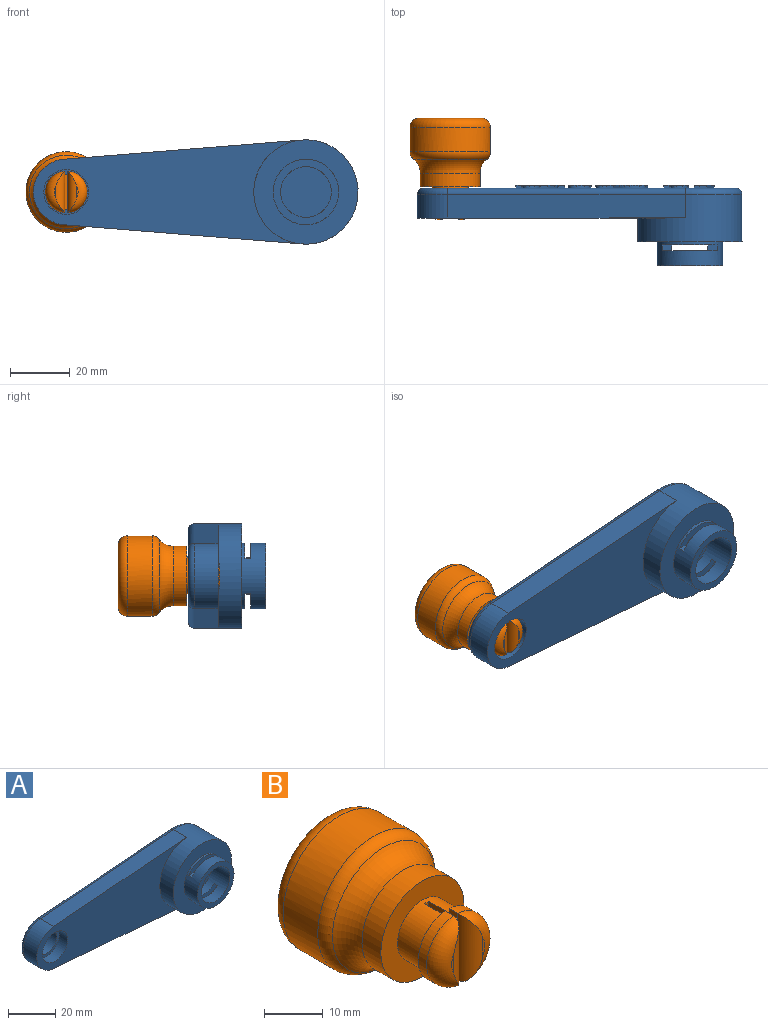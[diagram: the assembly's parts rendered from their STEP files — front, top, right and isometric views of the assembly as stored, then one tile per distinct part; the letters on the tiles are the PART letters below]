
ASSEMBLY  parts=2 mates=1
PART A: 165 faces, bbox 111.3x27x37.9 mm
  f0: plane 104.91x31mm, normal (0,1,0), area 2040.8mm2, adj f22,f23,f24,f25,f27,f28,f29,f30
  f1: cylinder r=7.5mm len=15mm, axis (0,1,0), area 235.6mm2, adj f8,f26
  f2: cylinder r=11mm len=22mm, axis (0,1,0), area 466.1mm2, adj f9,f10,f12,f13,f14,f16,f17,f18
  f3: cylinder r=8.5mm len=17mm, axis (0,1,0), area 534mm2, adj f10,f11,f13,f14,f15,f16,f18,f19
  f4: cylinder r=17.5mm len=35mm, axis (0,1,0), area 1344.7mm2, adj f5,f7,f8,f9,f22
  f5: plane 79.73x8mm, normal (-0.08,0,1), area 639.9mm2, adj f4,f6,f8,f23
  f6: cylinder r=11mm len=21.93mm, axis (0,1,0), area 262.2mm2, adj f5,f7,f8,f25
  f7: plane 79.73x8mm, normal (-0.08,0,-1), area 639.9mm2, adj f4,f6,f8,f24
  f8: plane 89.84x34.86mm, normal (0,-1,0), area 1831.5mm2, adj f1,f4,f5,f6,f7
  f9: plane 35x35mm, normal (0,-1,0), area 582mm2, adj f2,f4
  f10: plane 22x22mm, normal (0,-1,0), area 153.2mm2, adj f2,f3
  f11: plane 17x17mm, normal (0,-1,0), area 227mm2, adj f3
  f12: plane 2x0.14mm, normal (-1,0,0), area 0.3mm2, adj f2,f13,f14,f15
  f13: plane 18.35x5mm, normal (0,-1,0), area 44.2mm2, adj f2,f3,f12,f15,f16
  f14: plane 18.35x5mm, normal (0,1,0), area 44.2mm2, adj f2,f3,f12,f15,f16
  f15: plane 3.11x2mm, normal (0,0,-1), area 6.2mm2, adj f3,f12,f13,f14
  f16: plane 3.2x2mm, normal (0,0,-1), area 6.4mm2, adj f2,f3,f13,f14
  f17: plane 2x0.14mm, normal (-1,0,0), area 0.3mm2, adj f2,f18,f19,f21
  f18: plane 18.35x5mm, normal (0,-1,0), area 44.2mm2, adj f2,f3,f17,f20,f21
  f19: plane 18.35x5mm, normal (0,1,0), area 44.2mm2, adj f2,f3,f17,f20,f21
  f20: plane 3.2x2mm, normal (0,0,1), area 6.4mm2, adj f2,f3,f18,f19
  f21: plane 3.11x2mm, normal (0,0,1), area 6.2mm2, adj f3,f17,f18,f19
  f22: torus R=15.5mm, axis (0,-1,0), area 175.1mm2, adj f0,f4,f23,f24
  f23: cylinder r=2mm len=79.9mm, axis (-1,0,-0.08), area 251.3mm2, adj f0,f5,f22,f25
  f24: cylinder r=2mm len=79.9mm, axis (1,0,-0.08), area 251.3mm2, adj f0,f7,f22,f25
  f25: torus R=9mm, axis (0,-1,0), area 96.2mm2, adj f0,f6,f23,f24
  f26: plane 15x15mm, normal (0,-1,0), area 63.6mm2, adj f1,f27
  f27: cylinder r=6mm len=12mm, axis (0,-1,0), area 188.5mm2, adj f0,f26
  f28: plane 11.28x2.38mm, normal (0.98,0,0.21), area 11.5mm2, adj f0,f29,f33,f34
  f29: plane 6.3x1mm, normal (0,0,-1), area 6.3mm2, adj f0,f28,f30,f34
  f30: plane 1.97x1mm, normal (-0.98,0,-0.21), area 2mm2, adj f0,f29,f31,f34
  f31: plane 3.95x1mm, normal (0,0,1), area 3.9mm2, adj f0,f30,f32,f34
  f32: plane 9.3x1.97mm, normal (-0.98,0,-0.21), area 9.5mm2, adj f0,f31,f33,f34
  f33: plane 2.36x1mm, normal (0,0,1), area 2.4mm2, adj f0,f28,f32,f34
  f34: plane 11.28x6.72mm, normal (0,1,0), area 34.4mm2, adj f28,f29,f30,f31,f32,f33
  f35: extruded ~1.02x1mm, area 1.2mm2, adj f36,f59,f60,f61
  f36: extruded ~1x0.74mm, area 0.8mm2, adj f35,f37,f60,f61
  f37: extruded ~1.02x1mm, area 1.1mm2, adj f36,f38,f60,f61
  f38: extruded ~1.8x1mm, area 1.8mm2, adj f37,f39,f60,f61
  f39: extruded ~1.47x1mm, area 1.7mm2, adj f38,f40,f60,f61
  f40: extruded ~1x1mm, area 1.2mm2, adj f39,f41,f60,f61
  f41: extruded ~1x0.78mm, area 0.9mm2, adj f40,f42,f60,f61
  f42: extruded ~1x0.91mm, area 1mm2, adj f41,f43,f60,f61
  f43: extruded ~2x1mm, area 2mm2, adj f42,f59,f60,f61
  f44: extruded ~1.79x1mm, area 2mm2, adj f0,f45,f58,f60
  f45: extruded ~2.46x1.27mm, area 2.9mm2, adj f0,f44,f46,f60
  f46: plane 1x0.03mm, normal (0,0,-1), area 0mm2, adj f0,f45,f47,f60
  f47: plane 1.12x1mm, normal (1,0,0.1), area 1.1mm2, adj f0,f46,f48,f60
  f48: plane 1.77x1mm, normal (0,0,-1), area 1.8mm2, adj f0,f47,f49,f60
  f49: plane 8.62x1.84mm, normal (-0.98,0,-0.21), area 8.8mm2, adj f0,f48,f50,f60
  f50: plane 1.79x1mm, normal (0,0,1), area 1.8mm2, adj f0,f49,f51,f60
  f51: plane 1.1x1mm, normal (0.93,0,0.37), area 1.2mm2, adj f0,f50,f52,f60
  f52: plane 1x0.06mm, normal (0,0,1), area 0.1mm2, adj f0,f51,f53,f60
  f53: extruded ~1x0.94mm, area 1.3mm2, adj f0,f52,f54,f60
  f54: extruded ~1.29x1mm, area 1.3mm2, adj f0,f53,f55,f60
  f55: extruded ~1.98x1mm, area 2.2mm2, adj f0,f54,f56,f60
  f56: extruded ~2.14x1.46mm, area 2.6mm2, adj f0,f55,f57,f60
  f57: extruded ~2.91x1mm, area 3mm2, adj f0,f56,f58,f60
  f58: extruded ~2.3x1mm, area 2.4mm2, adj f0,f44,f57,f60
  f59: extruded ~1.4x1mm, area 1.6mm2, adj f35,f43,f60,f61
  f60: plane 8.94x8.42mm, normal (0,1,0), area 46.1mm2, adj f35,f36,f37,f38,f39,f40,f41,f42
  f61: plane 5.18x3.12mm, normal (0,1,0), area 12mm2, adj f35,f36,f37,f38,f39,f40,f41,f42
  f62: extruded ~1.83x1mm, area 2mm2, adj f0,f63,f79,f80
  f63: extruded ~1.06x1mm, area 1.1mm2, adj f0,f62,f64,f80
  f64: extruded ~1.35x1mm, area 1.5mm2, adj f0,f63,f65,f80
  f65: plane 1.93x1mm, normal (-0.9,0,-0.43), area 2.1mm2, adj f0,f64,f66,f80
  f66: extruded ~1.6x1mm, area 1.7mm2, adj f0,f65,f67,f80
  f67: extruded ~1.71x1mm, area 1.7mm2, adj f0,f66,f68,f80
  f68: extruded ~3.09x1mm, area 3.3mm2, adj f0,f67,f69,f80
  f69: extruded ~2.58x2.14mm, area 3.4mm2, adj f0,f68,f70,f80
  f70: extruded ~3.72x1mm, area 3.8mm2, adj f0,f69,f71,f80
  f71: extruded ~3.27x1.09mm, area 3.5mm2, adj f0,f70,f72,f80
  f72: extruded ~3.05x1.15mm, area 3.4mm2, adj f0,f71,f73,f80
  f73: extruded ~3.09x1mm, area 3.2mm2, adj f0,f72,f74,f80
  f74: plane 2.01x1mm, normal (-1,0,0), area 2mm2, adj f0,f73,f75,f80
  f75: extruded ~2.61x1mm, area 2.7mm2, adj f0,f74,f76,f80
  f76: extruded ~1.69x1mm, area 1.9mm2, adj f0,f75,f77,f80
  f77: extruded ~1.91x1mm, area 2mm2, adj f0,f76,f78,f80
  f78: extruded ~2.61x1mm, area 2.7mm2, adj f0,f77,f79,f80
  f79: extruded ~1.84x1.31mm, area 2.3mm2, adj f0,f62,f78,f80
  f80: plane 11.61x9.35mm, normal (0,1,0), area 43.6mm2, adj f62,f63,f64,f65,f66,f67,f68,f69
  f81: plane 2.32x1mm, normal (0,0,-1), area 2.3mm2, adj f0,f82,f99,f100
  f82: plane 4.91x1.03mm, normal (-0.98,0,-0.2), area 5mm2, adj f0,f81,f83,f100
  f83: extruded ~1.39x1mm, area 1.4mm2, adj f0,f82,f84,f100
  f84: extruded ~1.84x1mm, area 2mm2, adj f0,f83,f85,f100
  f85: extruded ~1.65x1mm, area 1.8mm2, adj f0,f84,f86,f100
  f86: extruded ~1.36x1mm, area 1.4mm2, adj f0,f85,f87,f100
  f87: extruded ~1.07x1mm, area 1.4mm2, adj f0,f86,f88,f100
  f88: plane 1x0.06mm, normal (0,0,1), area 0.1mm2, adj f0,f87,f89,f100
  f89: extruded ~2.38x1mm, area 2.5mm2, adj f0,f88,f90,f100
  f90: extruded ~2.14x1mm, area 2.2mm2, adj f0,f89,f91,f100
  f91: plane 2.32x1mm, normal (0,0,1), area 2.3mm2, adj f0,f90,f92,f100
  f92: plane 12x2.54mm, normal (0.98,0,0.21), area 12.3mm2, adj f0,f91,f93,f100
  f93: plane 2.32x1mm, normal (0,0,-1), area 2.3mm2, adj f0,f92,f94,f100
  f94: plane 3.57x1mm, normal (-0.98,0,-0.21), area 3.7mm2, adj f0,f93,f95,f100
  f95: extruded ~2.45x1mm, area 2.6mm2, adj f0,f94,f96,f100
  f96: extruded ~1.29x1mm, area 1.6mm2, adj f0,f95,f97,f100
  f97: extruded ~1x0.95mm, area 1.4mm2, adj f0,f96,f98,f100
  f98: extruded ~1x0.92mm, area 0.9mm2, adj f0,f97,f99,f100
  f99: plane 5.04x1.06mm, normal (0.98,0,0.21), area 5.1mm2, adj f0,f81,f98,f100
  f100: plane 12x8.45mm, normal (0,1,0), area 51.5mm2, adj f81,f82,f83,f84,f85,f86,f87,f88
  f101: extruded ~2.52x1mm, area 2.7mm2, adj f0,f102,f124,f125
  f102: extruded ~3.01x1mm, area 3.1mm2, adj f0,f101,f103,f125
  f103: plane 1.75x1mm, normal (-1,0,0), area 1.8mm2, adj f0,f102,f104,f125
  f104: extruded ~1.33x1mm, area 1.4mm2, adj f0,f103,f105,f125
  f105: extruded ~1.22x1mm, area 1.2mm2, adj f0,f104,f106,f125
  f106: extruded ~1.14x1mm, area 1.2mm2, adj f0,f105,f107,f125
  f107: extruded ~1.11x1mm, area 1.2mm2, adj f0,f106,f108,f125
  f108: plane 1x0.16mm, normal (-1,0,0), area 0.2mm2, adj f0,f107,f109,f125
  f109: plane 1x0.16mm, normal (-1,0,-0.09), area 0.2mm2, adj f0,f108,f110,f125
  f110: plane 1x0.4mm, normal (0,0,-1), area 0.4mm2, adj f0,f109,f111,f125
  f111: extruded ~3.68x1mm, area 3.8mm2, adj f0,f110,f112,f125
  f112: extruded ~2.22x1.29mm, area 2.7mm2, adj f0,f111,f113,f125
  f113: extruded ~1.72x1mm, area 2mm2, adj f0,f112,f114,f125
  f114: extruded ~2.13x1mm, area 2.3mm2, adj f0,f113,f115,f125
  f115: extruded ~2.46x1mm, area 2.6mm2, adj f0,f114,f116,f125
  f116: extruded ~2.01x1.72mm, area 2.7mm2, adj f0,f115,f117,f125
  f117: extruded ~2.91x1mm, area 3mm2, adj f0,f116,f124,f125
  f118: extruded ~1.28x1mm, area 1.5mm2, adj f119,f123,f125,f126
  f119: extruded ~1x0.81mm, area 1.3mm2, adj f118,f120,f125,f126
  f120: extruded ~1.01x1mm, area 1.3mm2, adj f119,f121,f125,f126
  f121: extruded ~1.86x1mm, area 1.9mm2, adj f120,f122,f125,f126
  f122: plane 1x0.35mm, normal (0,0,1), area 0.3mm2, adj f121,f123,f125,f126
  f123: extruded ~1.5x1mm, area 1.7mm2, adj f118,f122,f125,f126
  f124: extruded ~2.46x1mm, area 2.7mm2, adj f0,f101,f117,f125
  f125: plane 8.94x7.71mm, normal (0,1,0), area 41.7mm2, adj f101,f102,f103,f104,f105,f106,f107,f108
  f126: plane 2.88x2.12mm, normal (0,1,0), area 4.2mm2, adj f118,f119,f120,f121,f122,f123
  f127: extruded ~1.72x1mm, area 1.9mm2, adj f0,f128,f136,f137
  f128: plane 1x0.05mm, normal (0,0,1), area 0mm2, adj f0,f127,f129,f137
  f129: extruded ~1.78x1mm, area 1.8mm2, adj f0,f128,f130,f137
  f130: plane 4.52x1mm, normal (-1,0,0.08), area 4.5mm2, adj f0,f129,f131,f137
  f131: plane 2.28x1mm, normal (0,0,1), area 2.3mm2, adj f0,f130,f132,f137
  f132: plane 8.62x1.06mm, normal (0.99,0,-0.12), area 8.7mm2, adj f0,f131,f133,f137
  f133: plane 2.49x1mm, normal (0,0,-1), area 2.5mm2, adj f0,f132,f134,f137
  f134: plane 8.62x4.66mm, normal (-0.88,0,-0.48), area 9.8mm2, adj f0,f133,f135,f137
  f135: plane 2.49x1mm, normal (0,0,1), area 2.5mm2, adj f0,f134,f136,f137
  f136: plane 4.58x2.29mm, normal (0.89,0,0.45), area 5.1mm2, adj f0,f127,f135,f137
  f137: plane 8.62x8.21mm, normal (0,1,0), area 35.7mm2, adj f127,f128,f129,f130,f131,f132,f133,f134
  f138: extruded ~1.02x1mm, area 1.2mm2, adj f139,f162,f163,f164
  f139: extruded ~1x0.74mm, area 0.8mm2, adj f138,f140,f163,f164
  f140: extruded ~1.02x1mm, area 1.1mm2, adj f139,f141,f163,f164
  f141: extruded ~1.8x1mm, area 1.8mm2, adj f140,f142,f163,f164
  f142: extruded ~1.47x1mm, area 1.7mm2, adj f141,f143,f163,f164
  f143: extruded ~1x1mm, area 1.2mm2, adj f142,f144,f163,f164
  f144: extruded ~1x0.78mm, area 0.9mm2, adj f143,f145,f163,f164
  f145: extruded ~1x0.91mm, area 1mm2, adj f144,f146,f163,f164
  f146: extruded ~2x1mm, area 2mm2, adj f145,f162,f163,f164
  f147: extruded ~1.79x1mm, area 2mm2, adj f0,f148,f161,f163
  f148: extruded ~2.46x1.27mm, area 2.9mm2, adj f0,f147,f149,f163
  f149: plane 1x0.03mm, normal (0,0,-1), area 0mm2, adj f0,f148,f150,f163
  f150: plane 1.12x1mm, normal (1,0,0.1), area 1.1mm2, adj f0,f149,f151,f163
  f151: plane 1.77x1mm, normal (0,0,-1), area 1.8mm2, adj f0,f150,f152,f163
  f152: plane 8.62x1.84mm, normal (-0.98,0,-0.21), area 8.8mm2, adj f0,f151,f153,f163
  f153: plane 1.79x1mm, normal (0,0,1), area 1.8mm2, adj f0,f152,f154,f163
  f154: plane 1.1x1mm, normal (0.93,0,0.37), area 1.2mm2, adj f0,f153,f155,f163
  f155: plane 1x0.06mm, normal (0,0,1), area 0.1mm2, adj f0,f154,f156,f163
  f156: extruded ~1x0.94mm, area 1.3mm2, adj f0,f155,f157,f163
  f157: extruded ~1.29x1mm, area 1.3mm2, adj f0,f156,f158,f163
  f158: extruded ~1.98x1mm, area 2.2mm2, adj f0,f157,f159,f163
  f159: extruded ~2.14x1.46mm, area 2.6mm2, adj f0,f158,f160,f163
  f160: extruded ~2.91x1mm, area 3mm2, adj f0,f159,f161,f163
  f161: extruded ~2.3x1mm, area 2.4mm2, adj f0,f147,f160,f163
  f162: extruded ~1.4x1mm, area 1.6mm2, adj f138,f146,f163,f164
  f163: plane 8.94x8.42mm, normal (0,1,0), area 46.1mm2, adj f138,f139,f140,f141,f142,f143,f144,f145
  f164: plane 5.18x3.12mm, normal (0,1,0), area 12mm2, adj f138,f139,f140,f141,f142,f143,f144,f145
PART B: 21 faces, bbox 34.6x34x34.6 mm
  f0: cylinder r=7mm len=13.96mm, axis (0,1,0), area 42mm2, adj f5,f15,f19
  f1: cylinder r=6mm len=12mm, axis (0,-1,0), area 216.2mm2, adj f4,f5,f7,f14,f15,f16
  f2: plane 3.87x0.5mm, normal (0,-1,0), area 1.3mm2, adj f17,f18
  f3: plane 3.87x0.5mm, normal (0,-1,0), area 1.3mm2, adj f19,f20
  f4: plane 13.96x6.5mm, normal (0,1,0), area 19.4mm2, adj f1,f13,f14
  f5: plane 13.96x6.5mm, normal (0,1,0), area 19.4mm2, adj f0,f1,f15
  f6: cylinder r=10mm len=20mm, axis (0,-1,0), area 285.6mm2, adj f7,f10
  f7: plane 20x20mm, normal (0,-1,0), area 201.1mm2, adj f1,f6
  f8: cylinder r=13.5mm len=27mm, axis (0,-1,0), area 706.6mm2, adj f11,f12
  f9: plane 21x21mm, normal (0,1,0), area 346.4mm2, adj f11
  f10: torus R=16mm, axis (0,1,0), area 371.9mm2, adj f6,f12
  f11: torus R=10.5mm, axis (0,1,0), area 367.4mm2, adj f8,f9
  f12: torus R=10.5mm, axis (0,-1,0), area 225.5mm2, adj f8,f10
  f13: cylinder r=7mm len=13.96mm, axis (0,1,0), area 42mm2, adj f4,f14,f18
  f14: plane 13.96x7mm, normal (1,0,0), area 87.7mm2, adj f1,f4,f13,f16,f17
  f15: plane 13.96x7mm, normal (-1,0,0), area 87.7mm2, adj f0,f1,f5,f16,f20
  f16: plane 12x1mm, normal (0,-1,0), area 12mm2, adj f1,f14,f15
  f17: cylinder r=3mm len=13.96mm, axis (0,0,1), area 52mm2, adj f2,f14,f18
  f18: torus R=4mm, axis (0,-1,0), area 71.7mm2, adj f2,f13,f17
  f19: torus R=4mm, axis (0,-1,0), area 71.7mm2, adj f0,f3,f20
  f20: cylinder r=3mm len=13.96mm, axis (0,0,-1), area 52mm2, adj f3,f15,f19
PLACE A t=(-8.8,7.76,6.51)mm
PLACE B t=(24.23,2.26,-35.62)mm
MATE revolute B.f0 <-> A.f1  axis (0,-1,0) through (-35.24,5.26,32.59)mm
